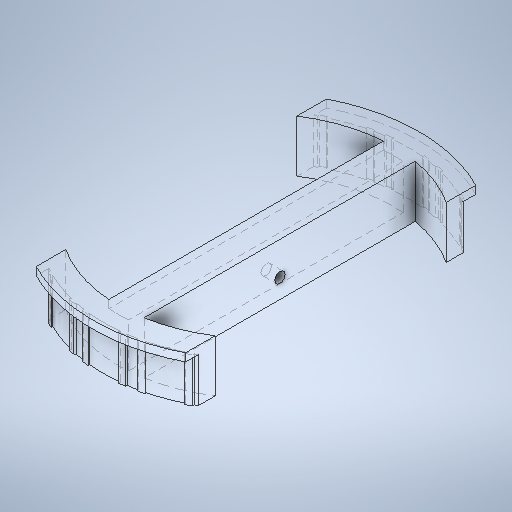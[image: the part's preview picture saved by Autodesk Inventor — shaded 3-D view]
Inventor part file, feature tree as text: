
AUTODESK INVENTOR PART (.ipt)
format: ipt  version: 2025 (Build 290162010, 162A)  size: 519,680 bytes
history: native  units: mm
features: sketch x10, extrude x9, pattern_circular x1, hole x1
ambient origin geometry x8: Origin, YZ Plane, XZ Plane, XY Plane, X Axis, Y Axis, Z Axis, Center Point
bodies: Solid1 (feature_tree)
feature tree (21):
  extrude  "Extrusion1"  Depth=15.0mm
  extrude  "Extrusion2"  Depth=5.0mm
  extrude  "Extrusion3"  TaperAngle=0.0deg  [1 undecoded]
  extrude  "Extrusion5"  Depth=78.1mm
  pattern_circular  "Circular Pattern1"  Count=18 Angle=360.0deg
  extrude  "Extrusion6"  Depth=83.0mm
  extrude  "Extrusion7"  Depth=13.75mm TaperAngle=0.0deg
  extrude  "Extrusion9"  Depth=70.0mm
  extrude  "Extrusion13"  Depth=10.0mm TaperAngle=0.0deg
  extrude  "Extrusion14"  Depth=2.0mm
  hole  "Hole3"  [1 undecoded]
  sketch  "Sketch1"  dims[d0=77.3mm d1=15.0mm]
  sketch  "Sketch2"  dims[d2=25.0mm d3=0.0mm d4=5.0mm]
  sketch  "Sketch3"  dims[d5=55.0mm d6=0.0mm d7=0.0mm]
  sketch  "Sketch9"  dims[d8=165.1mm d9=0.0mm d31=78.1mm]
  sketch  "Sketch11"  dims[d32=1.0mm d33=0.0mm d37=180.0mm d38=360.0deg]
  sketch  "Sketch12"  dims[d40=0.0mm d41=0.0mm d42=83.0mm]
  sketch  "Sketch14"  dims[d43=2.0mm d44=0.0mm d47=13.75mm d48=0.0mm]
  sketch  "Sketch18"  dims[d52=60.0mm d62=70.0mm]
  sketch  "Sketch19"  dims[d63=0.0mm d64=0.0mm d65=10.0mm d66=0.0mm]
  sketch  "Sketch20"  dims[d67=35.0mm d68=6.4mm d69=2.6416mm d70=7.01mm d71=4.0mm d72=2.0mm d73=90.0deg d74=10.979mm d75=0.0mm d56=0.5mm d57=0.872665mm d58=0.5mm d59=0.872665mm d60=0.872665mm d61=0.5mm]
note: 2 required parameter values undecoded (feature->parameter linkage not recoverable at this tier; creation-order binding heuristic only, values carry confidence <= 0.55)
